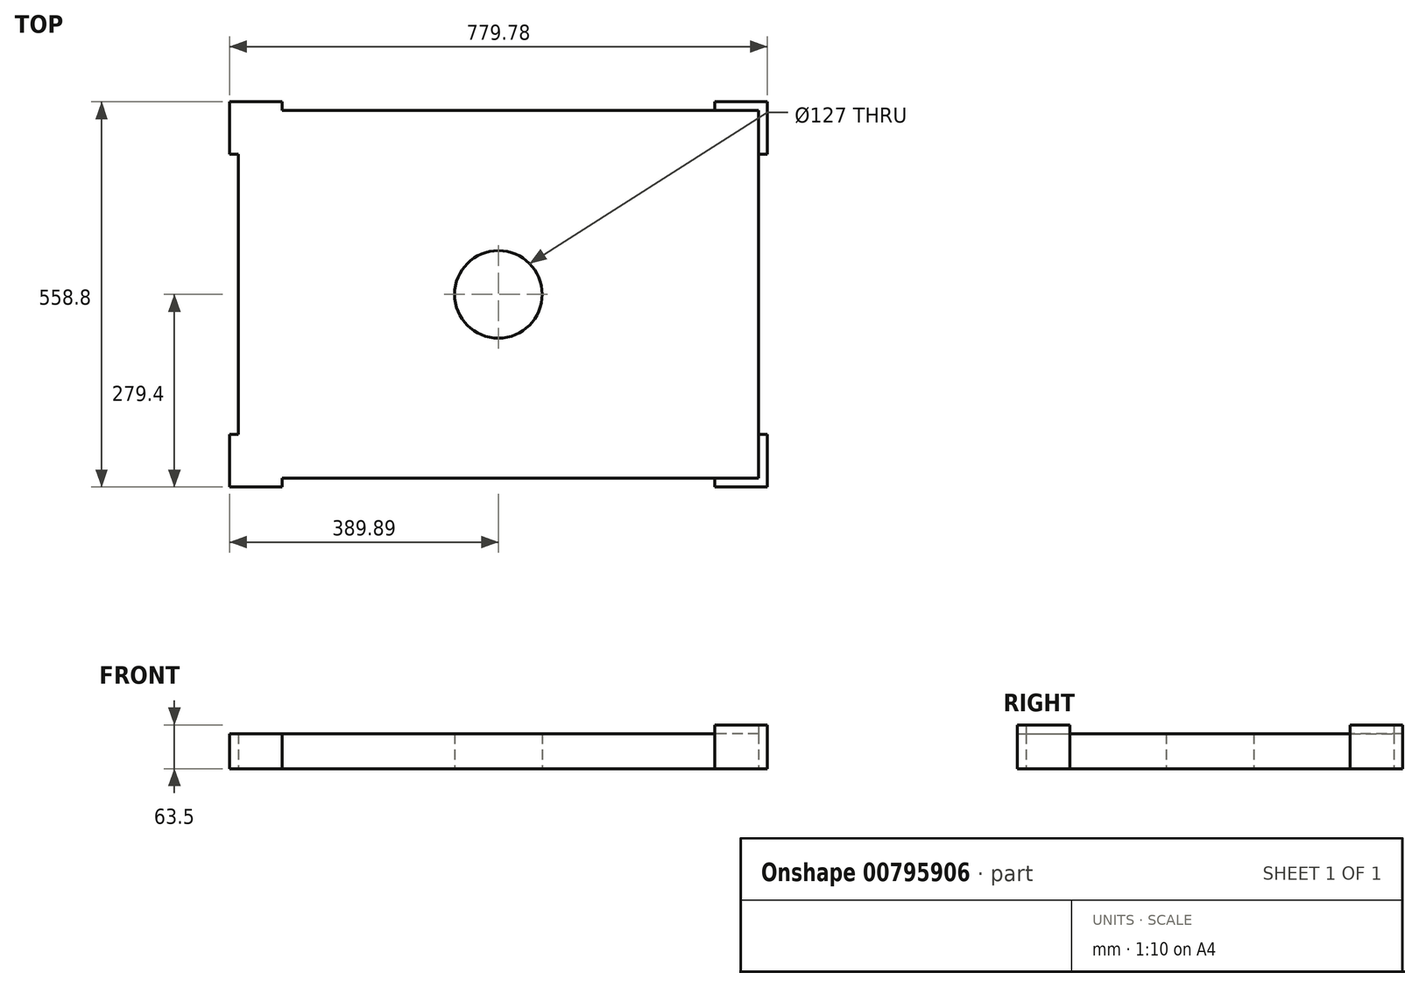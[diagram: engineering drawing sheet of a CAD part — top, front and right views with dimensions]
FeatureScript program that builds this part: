
annotation { "Feature Type Name" : "Feature", "Feature Type Description" : "" }
export const myFeature = defineFeature(function(context is Context, id is Id, definition is map)
    precondition{}
    {
        {
            var Q0;
            Q0=qCreatedBy(makeId("Top.planeOp"),FACE);
            var sketch = newSketch(context, id + "F0", { "sketchPlane" : qUnion([Q0])});
            skLineSegment(sketch, "E0.bottom", {"start": v(377.19, -266.7) * mm, "end": v(-377.2, -266.7) * mm});
            skLineSegment(sketch, "E0.top", {"start": v(377.19, 266.7) * mm, "end": v(-377.2, 266.7) * mm});
            skLineSegment(sketch, "E0.left", {"start": v(377.19, -266.7) * mm, "end": v(377.19, 266.7) * mm});
            skLineSegment(sketch, "E0.right", {"start": v(-377.2, -266.7) * mm, "end": v(-377.2, 266.7) * mm});
            skPoint(sketch, "E0.middle", {"position": v(0, 0) * mm});
            skCircle(sketch, "E1", {"center": v(0, 0) * mm, "radius": 63.5 * mm});
            skLineSegment(sketch, "E2.0", {"start": v(389.89, 279.4) * mm, "end": v(-389.9, 279.4) * mm});
            skLineSegment(sketch, "E2.1", {"start": v(389.89, -279.4) * mm, "end": v(389.89, 279.4) * mm});
            skLineSegment(sketch, "E2.2", {"start": v(389.89, -279.4) * mm, "end": v(-389.9, -279.4) * mm});
            skLineSegment(sketch, "E2.3", {"start": v(-389.9, -279.4) * mm, "end": v(-389.9, 279.4) * mm});
            skSolve(sketch);
        }
        {
            var Q0;
            Q0=qCreatedBy(makeId("Top.planeOp"),FACE);
            var sketch = newSketch(context, id + "F1", { "sketchPlane" : qUnion([Q0])});
            skLineSegment(sketch, "E3.bottom", {"start": v(-313.7, 279.4) * mm, "end": v(-389.9, 279.4) * mm});
            skLineSegment(sketch, "E3.right", {"start": v(-389.9, 279.4) * mm, "end": v(-389.9, 203.2) * mm});
            skPoint(sketch, "E3.middle", {"position": v(-377.2, 266.7) * mm});
            skLineSegment(sketch, "E4", {"start": v(-313.7, 279.4) * mm, "end": v(-313.7, 266.7) * mm});
            skLineSegment(sketch, "E5", {"start": v(-313.7, 266.7) * mm, "end": v(-377.2, 266.7) * mm});
            skLineSegment(sketch, "E6", {"start": v(-377.2, 203.2) * mm, "end": v(-389.9, 203.2) * mm});
            skLineSegment(sketch, "E7", {"start": v(-377.2, 266.7) * mm, "end": v(-377.2, 203.2) * mm});
            skLineSegment(sketch, "E8", {"start": v(0, 302.06) * mm, "end": v(0, -310.3) * mm, "construction": true});
            skLineSegment(sketch, "E9", {"start": v(-407.96, 0) * mm, "end": v(417.62, 0) * mm, "construction": true});
            skLineSegment(sketch, "E10.MirrorCS", {"start": v(-313.7, -279.4) * mm, "end": v(-313.7, -266.7) * mm});
            skLineSegment(sketch, "E11.MirrorCS", {"start": v(-377.2, -203.2) * mm, "end": v(-389.9, -203.2) * mm});
            skLineSegment(sketch, "E12.MirrorCS", {"start": v(-389.9, -279.4) * mm, "end": v(-389.9, -203.2) * mm});
            skLineSegment(sketch, "E13.MirrorCS", {"start": v(-377.2, -266.7) * mm, "end": v(-377.2, -203.2) * mm});
            skPoint(sketch, "E14.MirrorP", {"position": v(-377.2, -266.7) * mm});
            skLineSegment(sketch, "E15.MirrorCS", {"start": v(-313.7, -266.7) * mm, "end": v(-377.2, -266.7) * mm});
            skLineSegment(sketch, "E16.MirrorCS", {"start": v(-313.7, -279.4) * mm, "end": v(-389.9, -279.4) * mm});
            skLineSegment(sketch, "E17.MirrorCS", {"start": v(377.2, -203.2) * mm, "end": v(389.9, -203.2) * mm});
            skLineSegment(sketch, "E18.MirrorCS", {"start": v(313.7, -279.4) * mm, "end": v(313.7, -266.7) * mm});
            skLineSegment(sketch, "E19.MirrorCS", {"start": v(313.7, -266.7) * mm, "end": v(377.2, -266.7) * mm});
            skLineSegment(sketch, "E20.MirrorCS", {"start": v(313.7, -279.4) * mm, "end": v(389.9, -279.4) * mm});
            skLineSegment(sketch, "E21.MirrorCS", {"start": v(389.9, -279.4) * mm, "end": v(389.9, -203.2) * mm});
            skLineSegment(sketch, "E22.MirrorCS", {"start": v(377.2, -266.7) * mm, "end": v(377.2, -203.2) * mm});
            skPoint(sketch, "E23.MirrorP", {"position": v(377.2, -266.7) * mm});
            skLineSegment(sketch, "E24.MirrorCS", {"start": v(377.2, 203.2) * mm, "end": v(389.9, 203.2) * mm});
            skLineSegment(sketch, "E25.MirrorCS", {"start": v(313.7, 279.4) * mm, "end": v(313.7, 266.7) * mm});
            skLineSegment(sketch, "E26.MirrorCS", {"start": v(313.7, 279.4) * mm, "end": v(389.9, 279.4) * mm});
            skLineSegment(sketch, "E27.MirrorCS", {"start": v(377.2, 266.7) * mm, "end": v(377.2, 203.2) * mm});
            skPoint(sketch, "E28.MirrorP", {"position": v(377.2, 266.7) * mm});
            skLineSegment(sketch, "E29.MirrorCS", {"start": v(313.7, 266.7) * mm, "end": v(377.2, 266.7) * mm});
            skLineSegment(sketch, "E30.MirrorCS", {"start": v(389.9, 279.4) * mm, "end": v(389.9, 203.2) * mm});
            skSolve(sketch);
        }
        {
            var Q0;
            Q0=makeQuery(id+"F0.imprint","IMPRINT",FACE,{"disambiguationData":[TD([[makeQuery(id+"F0.imprint","IMPRINT",EDGE,{"derivedFrom":sQuery(id+"F0.wireOp",EDGE,"E0.bottom")}),-1.0]])]});
            extrude(context, id + "F2", {"entities" : qUnion([Q0]), "depth" : 50.8 * mm, "offsetDistance" : 25.4 * mm});
        }
        {
            var Q0;
            Q0=makeQuery(id+"F1.imprint","IMPRINT",FACE,{"disambiguationData":[TD([[makeQuery(id+"F1.imprint","IMPRINT",EDGE,{"derivedFrom":sQuery(id+"F1.wireOp",EDGE,"E10.MirrorCS")}),1.0]])]});
            var Q1;
            Q1=makeQuery(id+"F1.imprint","IMPRINT",FACE,{"disambiguationData":[TD([[makeQuery(id+"F1.imprint","IMPRINT",EDGE,{"derivedFrom":sQuery(id+"F1.wireOp",EDGE,"E3.bottom")}),1.0]])]});
            var Q2;
            Q2=makeQuery(id+"F2.opExtrude","CAP_FACE",FACE,{"disambiguationData":[OSD([sQuery(id+"F0.wireOp",EDGE,"E0.bottom"),sQuery(id+"F0.wireOp",EDGE,"E0.top"),sQuery(id+"F0.wireOp",EDGE,"E0.left"),sQuery(id+"F0.wireOp",EDGE,"E0.right"),sQuery(id+"F0.wireOp",EDGE,"E1")])],"isStart":false});
            extrude(context, id + "F3", {"entities" : qUnion([Q0, Q1]), "operationType" : NewBodyOperationType.ADD, "endBound" : BoundingType.UP_TO_SURFACE, "depth" : 50.8 * mm, "endBoundEntityFace" : qUnion([Q2]), "offsetDistance" : 25.4 * mm});
        }
        {
            var Q0;
            Q0=makeQuery(id+"F1.imprint","IMPRINT",FACE,{"disambiguationData":[TD([[makeQuery(id+"F1.imprint","IMPRINT",EDGE,{"derivedFrom":sQuery(id+"F1.wireOp",EDGE,"E17.MirrorCS")}),-1.0]])]});
            var Q1;
            Q1=makeQuery(id+"F1.imprint","IMPRINT",FACE,{"disambiguationData":[TD([[makeQuery(id+"F1.imprint","IMPRINT",EDGE,{"derivedFrom":sQuery(id+"F1.wireOp",EDGE,"E24.MirrorCS")}),1.0]])]});
            extrude(context, id + "F4", {"entities" : qUnion([Q0, Q1]), "operationType" : NewBodyOperationType.ADD, "depth" : 63.5 * mm, "offsetDistance" : 25.4 * mm});
        }
    });
